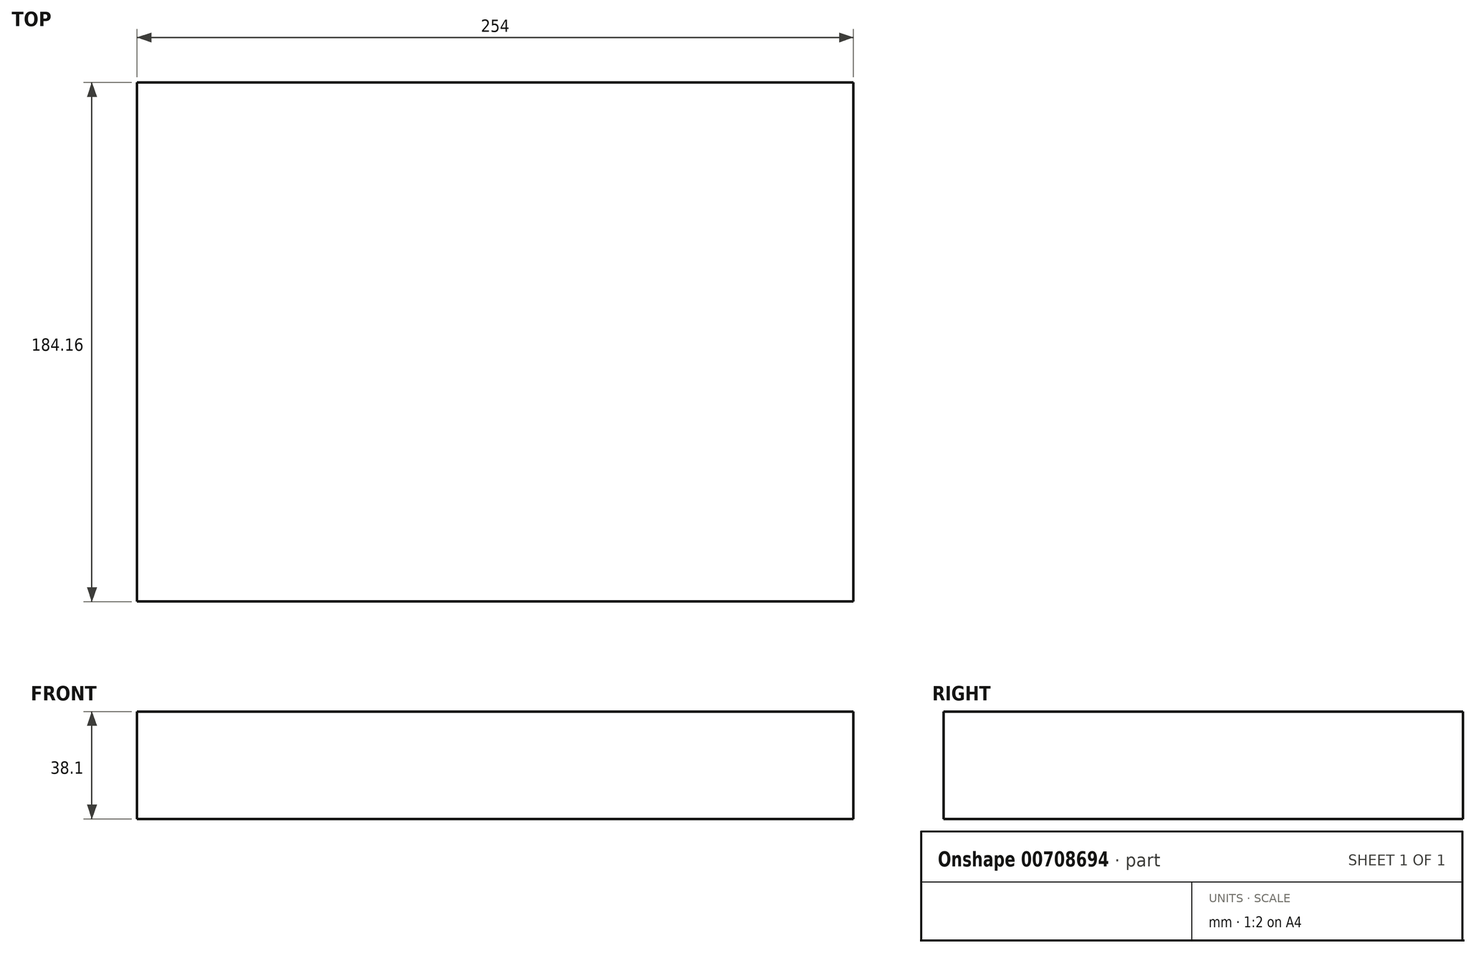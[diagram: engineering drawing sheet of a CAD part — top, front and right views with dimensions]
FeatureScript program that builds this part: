
annotation { "Feature Type Name" : "Feature", "Feature Type Description" : "" }
export const myFeature = defineFeature(function(context is Context, id is Id, definition is map)
    precondition{}
    {
        {
            var Q0;
            Q0=qCreatedBy(makeId("Right.planeOp"),FACE);
            var sketch = newSketch(context, id + "F0", { "sketchPlane" : qUnion([Q0])});
            skLineSegment(sketch, "E0.bottom", {"start": v(92.07, -19.05) * mm, "end": v(-92.08, -19.05) * mm});
            skLineSegment(sketch, "E0.top", {"start": v(92.08, 19.05) * mm, "end": v(-92.08, 19.05) * mm});
            skLineSegment(sketch, "E0.left", {"start": v(92.08, -19.05) * mm, "end": v(92.08, 19.05) * mm});
            skLineSegment(sketch, "E0.right", {"start": v(-92.08, -19.05) * mm, "end": v(-92.08, 19.05) * mm});
            skPoint(sketch, "E0.middle", {"position": v(0, 0) * mm});
            skSolve(sketch);
        }
        {
            var Q0;
            Q0=makeQuery(id+"F0.imprint","IMPRINT",FACE,{"disambiguationData":[TD([[makeQuery(id+"F0.imprint","IMPRINT",EDGE,{"derivedFrom":sQuery(id+"F0.wireOp",EDGE,"E0.bottom")}),-1.0]])]});
            extrude(context, id + "F1", {"entities" : qUnion([Q0]), "endBound" : BoundingType.SYMMETRIC, "depth" : 254 * mm, "offsetDistance" : 25.4 * mm});
        }
    });
